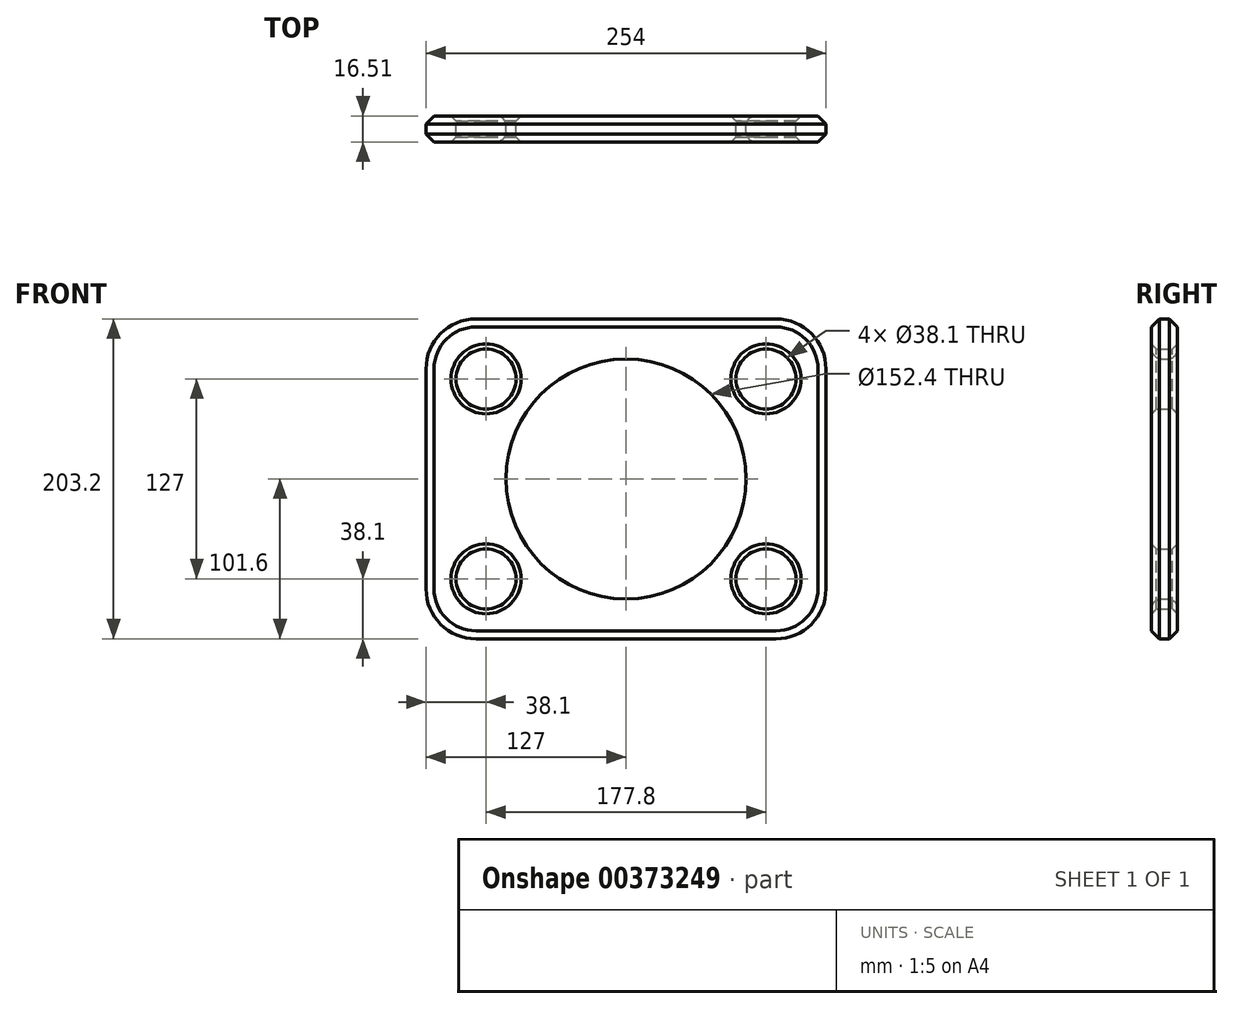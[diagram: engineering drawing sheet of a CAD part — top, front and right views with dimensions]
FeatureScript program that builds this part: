
annotation { "Feature Type Name" : "Feature", "Feature Type Description" : "" }
export const myFeature = defineFeature(function(context is Context, id is Id, definition is map)
    precondition{}
    {
        {
            var Q0;
            Q0=qCreatedBy(makeId("Front.planeOp"),FACE);
            var sketch = newSketch(context, id + "F0", { "sketchPlane" : qUnion([Q0])});
            skLineSegment(sketch, "E0.bottom", {"start": v(-95.25, 101.6) * mm, "end": v(95.25, 101.6) * mm});
            skLineSegment(sketch, "E0.top", {"start": v(-95.25, -101.6) * mm, "end": v(95.25, -101.6) * mm});
            skLineSegment(sketch, "E0.left", {"start": v(-127, 69.85) * mm, "end": v(-127, -69.85) * mm});
            skLineSegment(sketch, "E0.right", {"start": v(127, 69.85) * mm, "end": v(127, -69.85) * mm});
            skPoint(sketch, "E0.middle", {"position": v(0, 0) * mm});
            skCircle(sketch, "E1", {"center": v(0, 0) * mm, "radius": 76.2 * mm});
            skCircle(sketch, "E2", {"center": v(-88.9, 63.5) * mm, "radius": 19.05 * mm});
            skCircle(sketch, "E3.MirrorC", {"center": v(88.9, 63.5) * mm, "radius": 19.05 * mm});
            skCircle(sketch, "E4.MirrorC", {"center": v(-88.9, -63.5) * mm, "radius": 19.05 * mm});
            skCircle(sketch, "E5.MirrorC", {"center": v(88.9, -63.5) * mm, "radius": 19.05 * mm});
            skArc(sketch, "E6.filletArc", {"start": v(-95.25, 101.6) * mm, "mid": v(-117.7, 92.3) * mm, "end": v(-127, 69.85) * mm});
            skArc(sketch, "E7.filletArc", {"start": v(-127, -69.85) * mm, "mid": v(-117.7, -92.3) * mm, "end": v(-95.25, -101.6) * mm});
            skArc(sketch, "E8.filletArc", {"start": v(95.25, -101.6) * mm, "mid": v(117.7, -92.3) * mm, "end": v(127, -69.85) * mm});
            skArc(sketch, "E9.filletArc", {"start": v(127, 69.85) * mm, "mid": v(117.7, 92.3) * mm, "end": v(95.25, 101.6) * mm});
            skSolve(sketch);
        }
        {
            var Q0;
            Q0=makeQuery(id+"F0.imprint","IMPRINT",FACE,{"disambiguationData":[TD([[makeQuery(id+"F0.imprint","IMPRINT",EDGE,{"derivedFrom":sQuery(id+"F0.wireOp",EDGE,"E0.bottom")}),-1.0]])]});
            extrude(context, id + "F1", {"entities" : qUnion([Q0]), "depth" : 16.5 * mm});
        }
        {
            var Q0;
            Q0=makeQuery(id+"F1.opExtrude","CAP_EDGE",EDGE,{"disambiguationData":[OSD([sQuery(id+"F0.wireOp",EDGE,"E0.bottom")])],"isStart":false});
            var Q1;
            Q1=makeQuery(id+"F1.opExtrude","CAP_EDGE",EDGE,{"disambiguationData":[OSD([sQuery(id+"F0.wireOp",EDGE,"E6.filletArc")])],"isStart":false});
            chamfer(context, id + "F2", {"entities" : qUnion([Q0, Q1]), "width" : 5.08 * mm, "tangentPropagation" : true});
        }
        {
            var Q0;
            Q0=makeQuery(id+"F1.opExtrude","CAP_EDGE",EDGE,{"disambiguationData":[OSD([sQuery(id+"F0.wireOp",EDGE,"E0.right")])],"isStart":true});
            chamfer(context, id + "F3", {"entities" : qUnion([Q0]), "width" : 5.08 * mm, "tangentPropagation" : true});
        }
        {
            var Q0;
            Q0=makeQuery(id+"F1.opExtrude","CAP_EDGE",EDGE,{"disambiguationData":[OSD([sQuery(id+"F0.wireOp",EDGE,"E2")])],"isStart":false});
            var Q1;
            Q1=makeQuery(id+"F1.opExtrude","CAP_EDGE",EDGE,{"disambiguationData":[OSD([sQuery(id+"F0.wireOp",EDGE,"E3.MirrorC")])],"isStart":false});
            var Q2;
            Q2=makeQuery(id+"F1.opExtrude","CAP_EDGE",EDGE,{"disambiguationData":[OSD([sQuery(id+"F0.wireOp",EDGE,"E5.MirrorC")])],"isStart":false});
            var Q3;
            Q3=makeQuery(id+"F1.opExtrude","CAP_EDGE",EDGE,{"disambiguationData":[OSD([sQuery(id+"F0.wireOp",EDGE,"E4.MirrorC")])],"isStart":false});
            var Q4;
            Q4=makeQuery(id+"F1.opExtrude","CAP_EDGE",EDGE,{"disambiguationData":[OSD([sQuery(id+"F0.wireOp",EDGE,"E2")])],"isStart":true});
            var Q5;
            Q5=makeQuery(id+"F1.opExtrude","CAP_EDGE",EDGE,{"disambiguationData":[OSD([sQuery(id+"F0.wireOp",EDGE,"E3.MirrorC")])],"isStart":true});
            var Q6;
            Q6=makeQuery(id+"F1.opExtrude","CAP_EDGE",EDGE,{"disambiguationData":[OSD([sQuery(id+"F0.wireOp",EDGE,"E5.MirrorC")])],"isStart":true});
            var Q7;
            Q7=makeQuery(id+"F1.opExtrude","CAP_EDGE",EDGE,{"disambiguationData":[OSD([sQuery(id+"F0.wireOp",EDGE,"E4.MirrorC")])],"isStart":true});
            chamfer(context, id + "F4", {"entities" : qUnion([Q0, Q1, Q2, Q3, Q4, Q5, Q6, Q7]), "width" : 3.17 * mm, "tangentPropagation" : true});
        }
        {
            var Q0;
            Q0=makeQuery(id+"F1.opExtrude","CAP_EDGE",EDGE,{"disambiguationData":[OSD([sQuery(id+"F0.wireOp",EDGE,"E1")])],"isStart":true});
            var Q1;
            Q1=makeQuery(id+"F1.opExtrude","CAP_EDGE",EDGE,{"disambiguationData":[OSD([sQuery(id+"F0.wireOp",EDGE,"E1")])],"isStart":false});
            fillet(context, id + "F5", {"entities" : qUnion([Q0, Q1]), "radius" : 6.35 * mm, "tangentPropagation" : true, "allowEdgeOverflow" : false});
        }
    });
